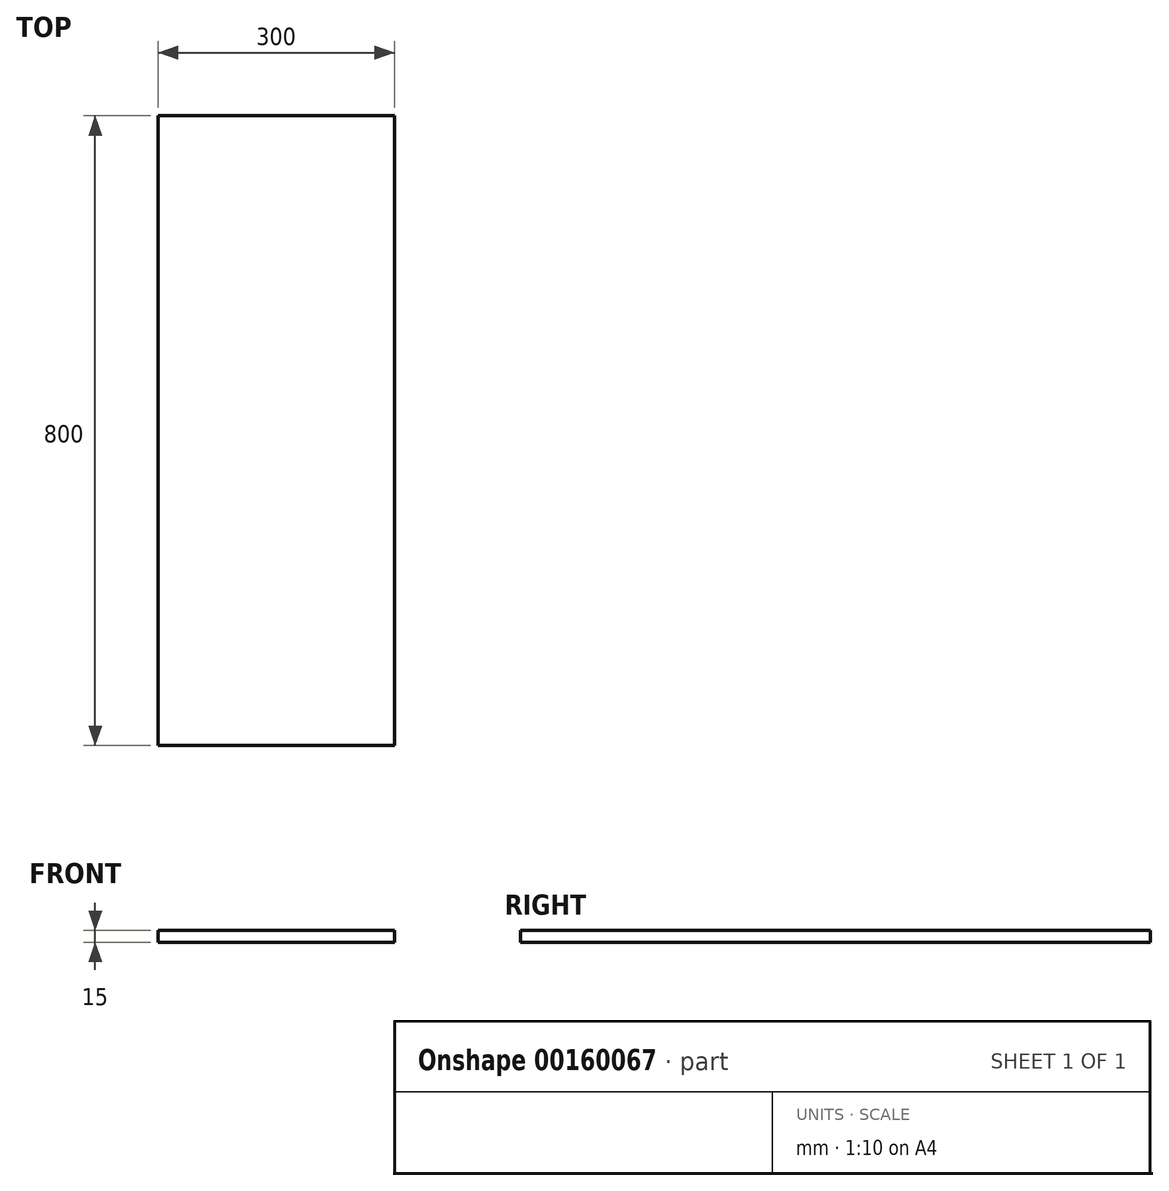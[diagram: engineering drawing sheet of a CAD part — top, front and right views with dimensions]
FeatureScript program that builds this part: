
annotation { "Feature Type Name" : "Feature", "Feature Type Description" : "" }
export const myFeature = defineFeature(function(context is Context, id is Id, definition is map)
    precondition{}
    {
        {
            var Q0;
            Q0=qCreatedBy(makeId("Top.planeOp"),FACE);
            var sketch = newSketch(context, id + "F0", { "sketchPlane" : qUnion([Q0])});
            skLineSegment(sketch, "E0.bottom", {"start": v(-101.18, 531.26) * mm, "end": v(198.82, 531.26) * mm});
            skLineSegment(sketch, "E0.top", {"start": v(-101.18, -268.74) * mm, "end": v(198.82, -268.74) * mm});
            skLineSegment(sketch, "E0.left", {"start": v(-101.18, 531.26) * mm, "end": v(-101.18, -268.74) * mm});
            skLineSegment(sketch, "E0.right", {"start": v(198.82, 531.26) * mm, "end": v(198.82, -268.74) * mm});
            skSolve(sketch);
        }
        {
            var Q0;
            Q0=makeQuery(id+"F0.imprint","IMPRINT",FACE,{"disambiguationData":[TD([[makeQuery(id+"F0.imprint","IMPRINT",EDGE,{"derivedFrom":sQuery(id+"F0.wireOp",EDGE,"E0.bottom")}),-1.0]])]});
            extrude(context, id + "F1", {"entities" : qUnion([Q0]), "depth" : 15 * mm});
        }
    });
